# Revit family: Faucet_Kitchen-DXV-Victorian-D35402150_Series
name_source: partatom
category: Plumbing Fixtures
revit_build: Autodesk Revit 2014 (Build: 20130308_1515(x64)
units: mm (PartAtom-declared; Revit-internal decimal feet)

## types (3) — shared parameters
ADA Compliant = Yes
Assembly Code = D2020300
CW Connection = Yes
CWFU = 1.5
Cold Water Connection Diameter = 3/8"
Default Elevation = 0"
Description = Victorian Pull-Out Kitchen Faucet
Flow Rate = 1.8 GPM (6.8L/min)
HW Connection = Yes
HWFU = 1.5
Height = 11 3/8"
Hot Water Connection Diameter = 0"
Installation Type = Deck Mounted
Length = 9 1/8"
Manufacturer = DXV
Price = Prices may vary. Please consult Manufacturer Representative for most up-to-date price list.
Product Documentation Link = https://dxv01.blob.core.windows.net
Product Page URL = http://www.dxv.com
Revised Date = 27/09/2017
URL = http://www.dxv.com
Vent Connection = No
WFU = 2
Warranty Documentation Link = https://www.dxv.com
Waste Connection = No
Width = 1 1/8"

## per-type parameters (varying)
| type | Finish | Material |
| D35402150.110 | Metal-DXV-110-Carbon Bronze | Metal-DXV-110-Carbon Bronze |
| D35402150.100 | Metal-DXV-100-Polished Chrome | Metal-DXV-100-Polished Chrome |
| D35402150.355 | Metal-DXV-355-Ultra Steel | Metal-DXV-355-Ultra Steel |

note: column(s) folded — value = type name in every type: Model

## geometry (parser evidence)
native form markers: Sweep x2
no freeform markers — native parametric forms only
